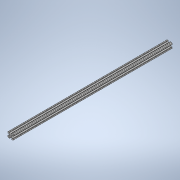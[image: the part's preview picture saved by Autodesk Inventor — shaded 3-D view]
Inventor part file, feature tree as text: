
AUTODESK INVENTOR PART (.ipt)
format: ipt  version: 2020 (Build 240168000, 168)  size: 239,616 bytes
history: native  units: in
note: dims shown in document units (in); Inventor stores cm internally (conversion verified against a paired STEP export)
features: extrude x1, sketch x1
ambient origin geometry x8: Origin, YZ Plane, XZ Plane, XY Plane, X Axis, Y Axis, Z Axis, Center Point
bodies: Solid1 (feature_tree)
feature tree (2):
  extrude  "Extrusion1"  [1 undecoded]
  sketch  "Sketch1"  dims[d0=29.0in d1=0.0in]
note: 1 required parameter value undecoded (feature->parameter linkage not recoverable at this tier; creation-order binding heuristic only, values carry confidence <= 0.55)
